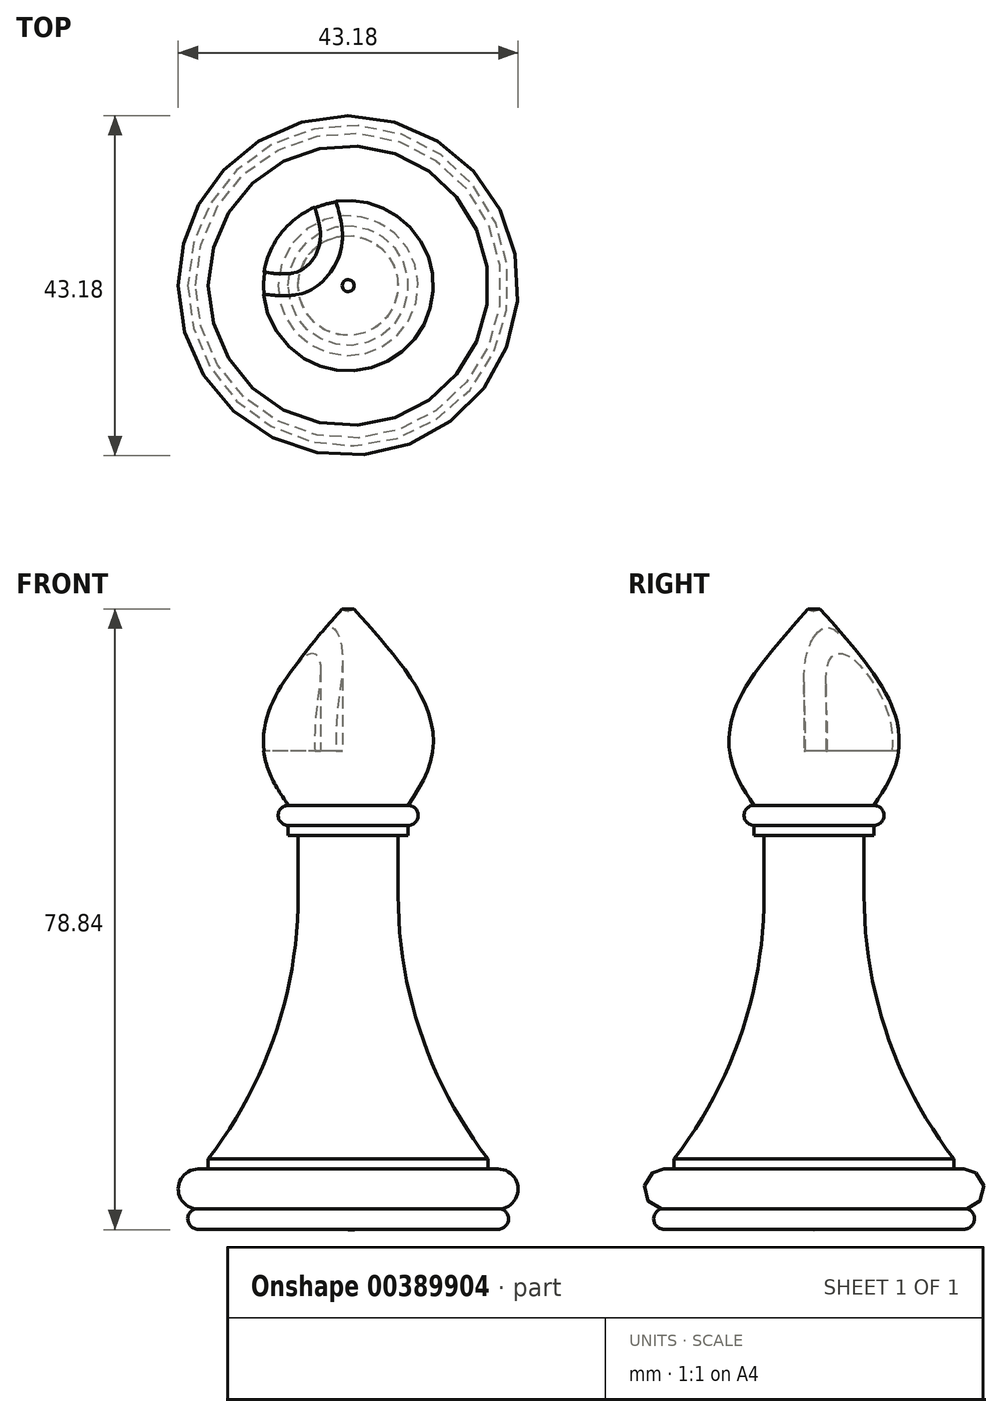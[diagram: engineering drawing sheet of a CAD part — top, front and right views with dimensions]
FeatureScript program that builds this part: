
annotation { "Feature Type Name" : "Feature", "Feature Type Description" : "" }
export const myFeature = defineFeature(function(context is Context, id is Id, definition is map)
    precondition{}
    {
        {
            var Q0;
            Q0=qCreatedBy(makeId("Front.planeOp"),FACE);
            var sketch = newSketch(context, id + "F0", { "sketchPlane" : qUnion([Q0])});
            skLineSegment(sketch, "E0", {"start": v(19.92, -0.03) * mm, "end": v(0.87, -0.08) * mm});
            skLineSegment(sketch, "E1", {"start": v(0.87, 0) * mm, "end": v(0.87, 81.28) * mm});
            skPoint(sketch, "E1.startSnap0", {"position": v(0.87, -0.08) * mm});
            skPoint(sketch, "E1.endSnap0", {"position": v(0.87, 5.08) * mm});
            skLineSegment(sketch, "E2", {"start": v(19.92, 2.54) * mm, "end": v(0.87, 2.54) * mm});
            skLineSegment(sketch, "E3", {"start": v(19.92, 7.62) * mm, "end": v(0.87, 7.62) * mm});
            skArc(sketch, "E4", {"start": v(19.92, 2.54) * mm, "mid": v(22.46, 5.08) * mm, "end": v(19.92, 7.62) * mm});
            skArc(sketch, "E5", {"start": v(19.92, -0.03) * mm, "mid": v(21.22, 1.11) * mm, "end": v(20.27, 2.56) * mm});
            skPoint(sketch, "E6.orphan", {"position": v(-18.18, -0.13) * mm});
            skLineSegment(sketch, "E7", {"start": v(18.65, 8.9) * mm, "end": v(18.65, 7.62) * mm});
            skPoint(sketch, "E8.startSnap0", {"position": v(10.4, 7.62) * mm});
            skLineSegment(sketch, "E9", {"start": v(0.87, 50) * mm, "end": v(8.49, 50) * mm});
            skPoint(sketch, "E10", {"position": v(7.22, 50) * mm});
            skLineSegment(sketch, "E11", {"start": v(7.22, 50) * mm, "end": v(7.22, 42.39) * mm});
            skArc(sketch, "E12", {"start": v(7.22, 42.39) * mm, "mid": v(10.15, 24.7) * mm, "end": v(18.65, 8.9) * mm});
            skLineSegment(sketch, "E13", {"start": v(8.49, 50) * mm, "end": v(8.49, 51.28) * mm});
            skLineSegment(sketch, "E14", {"start": v(8.49, 51.28) * mm, "end": v(0.87, 51.28) * mm});
            skLineSegment(sketch, "E15", {"start": v(8.49, 53.82) * mm, "end": v(0.87, 53.82) * mm});
            skArc(sketch, "E16", {"start": v(8.49, 51.28) * mm, "mid": v(9.76, 52.55) * mm, "end": v(8.49, 53.82) * mm});
            skPoint(sketch, "E8.start.orphan", {"position": v(10.4, 53.2) * mm});
            skLineSegment(sketch, "E17", {"start": v(1.64, 78.76) * mm, "end": v(0.87, 78.76) * mm});
            skFitSpline(sketch, "E18", {"points": [v(1.64, 78.76) * mm, v(10.78, 66.4) * mm, v(11.27, 59.12) * mm, v(8.49, 53.82) * mm], "startDerivative": vector(26.24, -29.45) * mm, "endDerivative": vector(-12.33, -18.64) * mm});
            skArc(sketch, "E19", {"start": v(1.64, 78.76) * mm, "mid": v(2.2, 80.3) * mm, "end": v(0.87, 81.28) * mm});
            skLineSegment(sketch, "E20", {"start": v(20.27, 2.56) * mm, "end": v(20.27, 2.56) * mm});
            skLineSegment(sketch, "E21", {"start": v(0.87, 0) * mm, "end": v(0.87, -0.08) * mm});
            skSolve(sketch);
        }
        {
            var Q0;
            Q0=qSketchRegion(id+"F0",true);
            var Q1;
            Q1=sQuery(id+"F0.wireOp",EDGE,"E1");
            revolve(context, id + "F1", {"entities" : qUnion([Q0]), "axis" : qUnion([Q1]), "revolveType" : RevolveType.FULL});
        }
        {
            var Q0;
            Q0=qCreatedBy(makeId("Top.planeOp"),FACE);
            cPlane(context, id + "F2", {"entities" : qUnion([Q0]), "cplaneType" : CPlaneType.OFFSET, "offset" : 98.55 * mm, "width" : 152.4 * mm, "height" : 152.4 * mm});
        }
        {
            var Q0;
            Q0=qCreatedBy(id+"F2.planeOp",FACE);
            var sketch = newSketch(context, id + "F3", { "sketchPlane" : qUnion([Q0])});
            skFitSpline(sketch, "E22", {"points": [v(-0.89, 11.34) * mm, v(0, 4.75) * mm, v(-4.05, -0.64) * mm, v(-10.73, -0.98) * mm], "startDerivative": vector(6.07, -19.82) * mm, "endDerivative": vector(-21.16, 2.74) * mm});
            skFitSpline(sketch, "E23.0", {"points": [v(-3.56, 10.52) * mm, v(-3.3, 9.7) * mm, v(-2.96, 8.54) * mm, v(-2.7, 7.2) * mm, v(-2.64, 6.47) * mm, v(-2.65, 5.93) * mm, v(-2.69, 5.55) * mm, v(-2.76, 5.18) * mm, v(-2.87, 4.8) * mm, v(-3.02, 4.4) * mm, v(-3.28, 3.87) * mm, v(-3.68, 3.22) * mm, v(-4.17, 2.67) * mm, v(-4.57, 2.31) * mm, v(-4.88, 2.09) * mm, v(-5.17, 1.92) * mm, v(-5.45, 1.79) * mm, v(-5.76, 1.68) * mm, v(-6.22, 1.58) * mm, v(-6.91, 1.5) * mm, v(-8.26, 1.52) * mm, v(-9.49, 1.67) * mm, v(-10.37, 1.79) * mm]});
            skLineSegment(sketch, "E24", {"start": v(-10.37, 1.79) * mm, "end": v(-10.73, -0.98) * mm});
            skLineSegment(sketch, "E25", {"start": v(-3.56, 10.52) * mm, "end": v(-0.89, 11.34) * mm});
            skSolve(sketch);
        }
        {
            var Q0;
            Q0=qSketchRegion(id+"F3",true);
            extrude(context, id + "F4", {"entities" : qUnion([Q0]), "operationType" : NewBodyOperationType.REMOVE, "oppositeDirection" : true, "depth" : 37.85 * mm});
        }
    });
